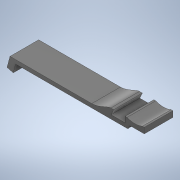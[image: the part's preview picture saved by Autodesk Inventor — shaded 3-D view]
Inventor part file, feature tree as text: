
AUTODESK INVENTOR PART (.ipt)
format: ipt  version: 2020 (Build 240168000, 168)  size: 180,224 bytes
history: native  units: mm
features: extrude x2, sketch x2, other x1, projected_geometry x1
ambient origin geometry x8: Origin, YZ Plane, XZ Plane, XY Plane, X Axis, Y Axis, Z Axis, Center Point
bodies: Body1 (feature_tree)
feature tree (6):
  other  "Твердое тело1"
  extrude  "Выдавливание1"  Depth=10.0mm
  extrude  "Выдавливание2"  Depth=3.0mm
  sketch  "Эскиз1"
  sketch  "Эскиз3"
  projected_geometry  "Спроецированная петля1"
